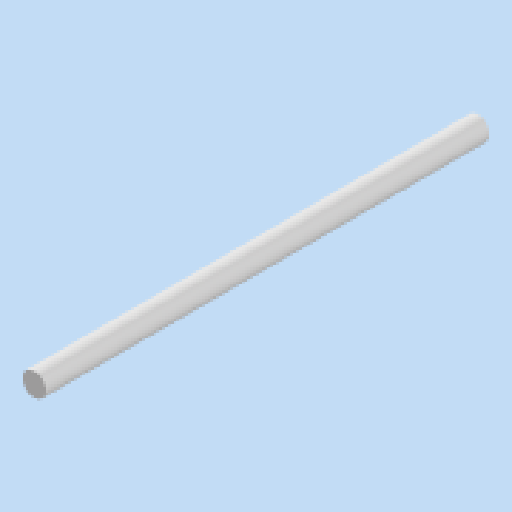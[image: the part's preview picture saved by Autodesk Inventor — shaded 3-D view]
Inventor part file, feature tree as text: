
AUTODESK INVENTOR PART (.ipt)
format: ipt  version: 2024 (Build 280153000, 153)  size: 83,968 bytes
history: native  units: in
note: dims shown in document units (in); Inventor stores cm internally (conversion verified against a paired STEP export)
features: extrude x1, sketch x1
ambient origin geometry x8: Origin, YZ Plane, XZ Plane, XY Plane, X Axis, Y Axis, Z Axis, Center Point
bodies: Solid1 (feature_tree)
feature tree (2):
  extrude  "Extrusion1"  Depth=6.0in TaperAngle=0.0deg
  sketch  "Sketch1"  dims[d0=0.315in d1=6.0in d2=0.0in]
